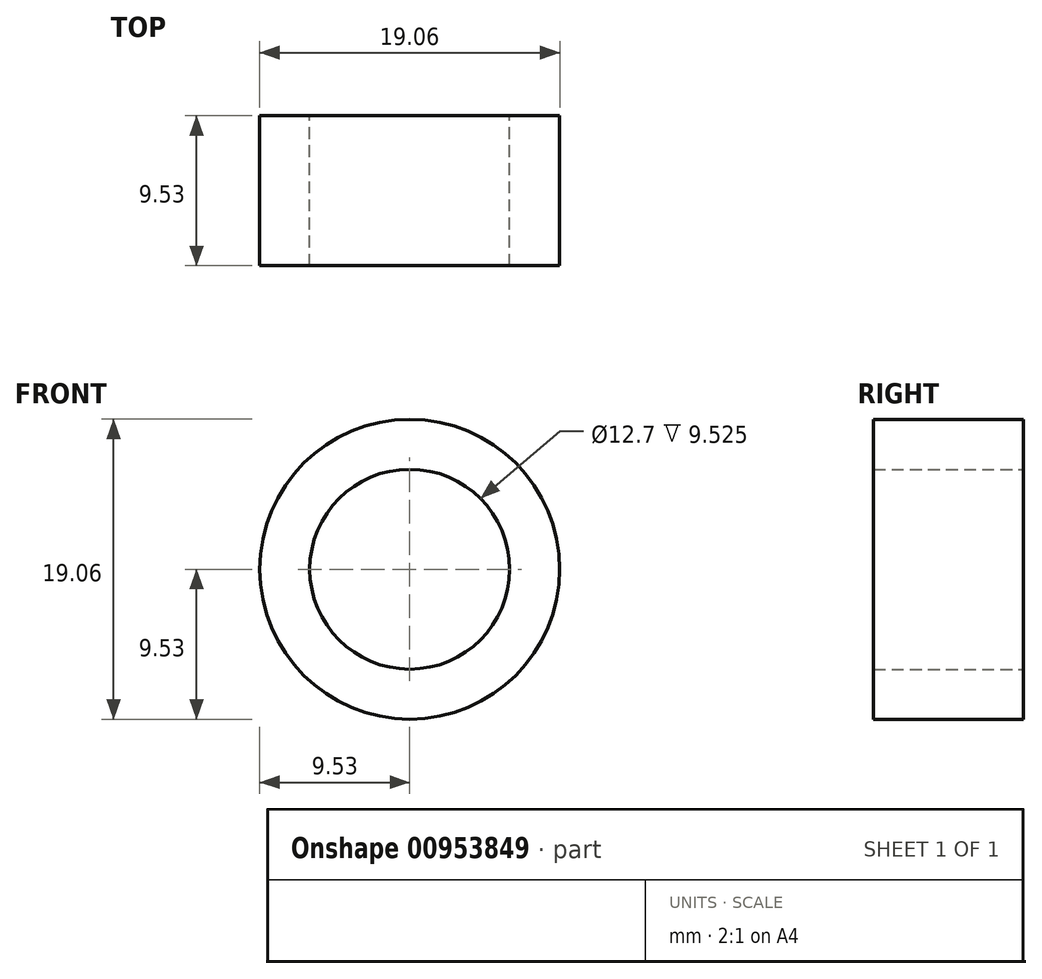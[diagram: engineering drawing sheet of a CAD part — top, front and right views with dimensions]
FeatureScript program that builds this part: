
annotation { "Feature Type Name" : "Feature", "Feature Type Description" : "" }
export const myFeature = defineFeature(function(context is Context, id is Id, definition is map)
    precondition{}
    {
        {
            var Q0;
            Q0=qCreatedBy(makeId("Front.planeOp"),FACE);
            var sketch = newSketch(context, id + "F0", { "sketchPlane" : qUnion([Q0])});
            skCircle(sketch, "E0", {"center": v(0, 0) * mm, "radius": 6.35 * mm});
            skCircle(sketch, "E1", {"center": v(0, 0) * mm, "radius": 9.53 * mm});
            skSolve(sketch);
        }
        {
            var Q0;
            Q0 = qSketchRegion(id + "F0", true);
            extrude(context, id + "F1", {"entities" : qUnion([Q0]), "depth" : 9.52 * mm, "offsetDistance" : 25.4 * mm});
        }
    });
